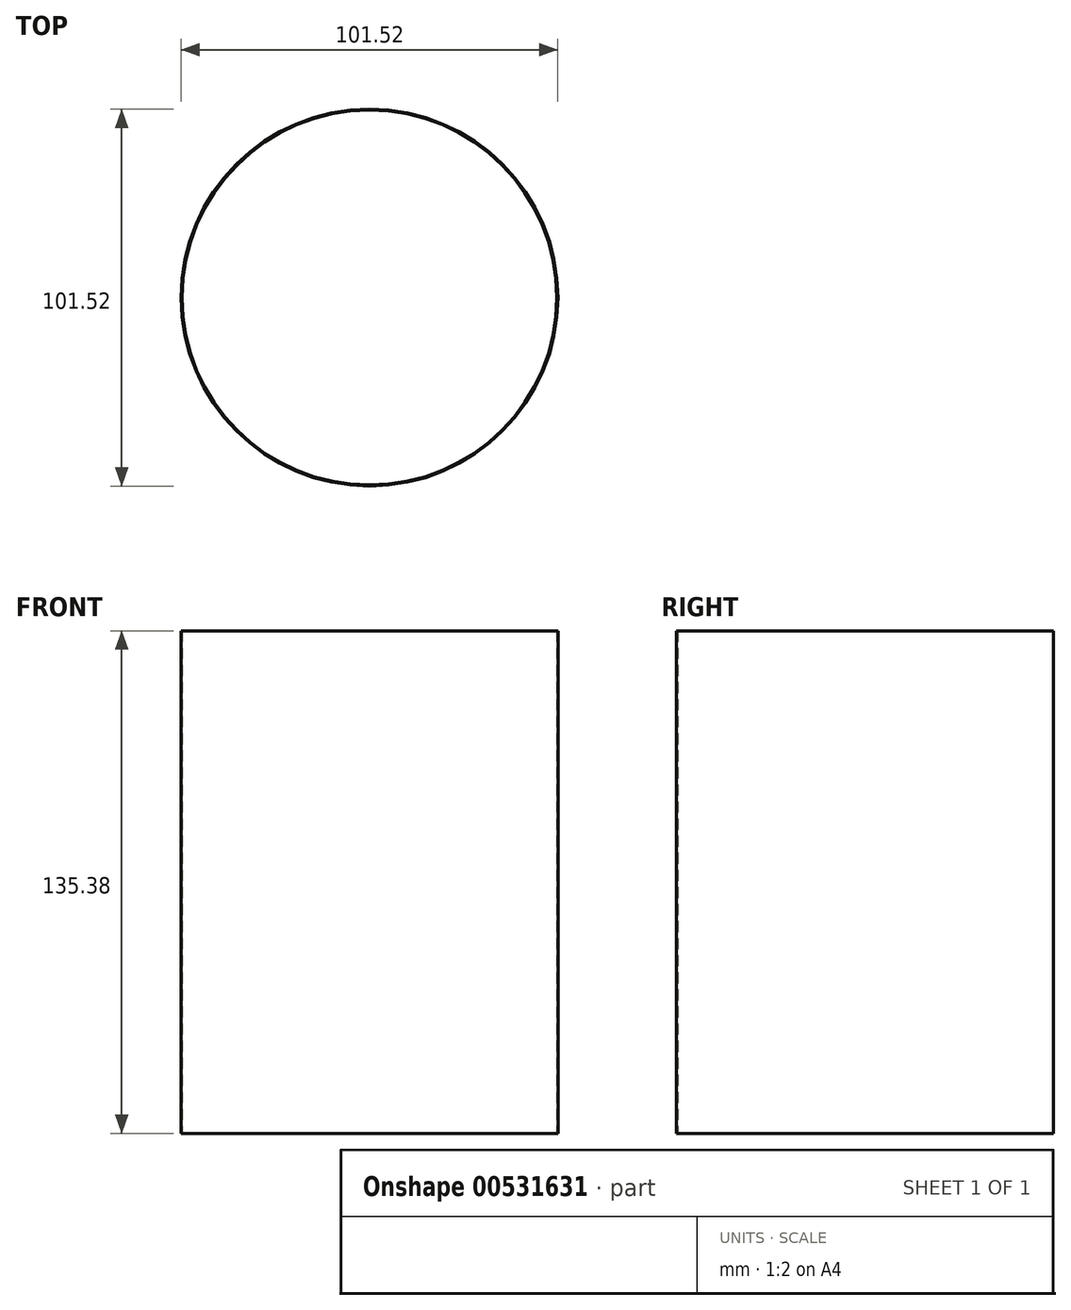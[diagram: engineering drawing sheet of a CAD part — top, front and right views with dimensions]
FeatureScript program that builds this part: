
annotation { "Feature Type Name" : "Feature", "Feature Type Description" : "" }
export const myFeature = defineFeature(function(context is Context, id is Id, definition is map)
    precondition{}
    {
        {
            var Q0;
            Q0=qCreatedBy(makeId("Top.planeOp"),FACE);
            var sketch = newSketch(context, id + "F0", { "sketchPlane" : qUnion([Q0])});
            skCircle(sketch, "E0", {"center": v(0, 0) * mm, "radius": 50.76 * mm});
            skCircle(sketch, "E1", {"center": v(0, 0) * mm, "radius": 50.5 * mm});
            skSolve(sketch);
        }
        {
            var Q0;
            Q0 = qSketchRegion(id + "F0", true);
            extrude(context, id + "F1", {"entities" : qUnion([Q0]), "depth" : 135.38 * mm, "offsetDistance" : 25.4 * mm});
        }
    });
